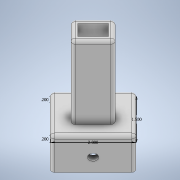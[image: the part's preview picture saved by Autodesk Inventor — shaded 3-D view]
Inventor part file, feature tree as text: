
AUTODESK INVENTOR PART (.ipt)
format: ipt  version: 2020 (Build 240168000, 168)  size: 212,480 bytes
history: native  units: in
note: dims shown in document units (in); Inventor stores cm internally (conversion verified against a paired STEP export)
features: sketch x4, extrude x4, hole x1, fillet x1
ambient origin geometry x8: Origin, YZ Plane, XZ Plane, XY Plane, X Axis, Y Axis, Z Axis, Center Point
bodies: Solid1 (feature_tree)
feature tree (10):
  sketch  "Sketch1"  dims[d0=1.5in d1=2.0in]
  extrude  "Extrusion1"  Depth=2.0in
  extrude  "Extrusion2"  Depth=0.2in
  hole  "Hole1"  [1 undecoded]
  extrude  "Extrusion3"  Depth=1.0in
  extrude  "Extrusion4"  Depth=0.7441in
  fillet  "Fillet1"  Radius=1.0276in
  sketch  "Sketch2"  dims[d2=0.2in d3=0.2in]
  sketch  "Sketch3"  dims[d4=1.0in d5=0.0in d6=0.2in d7=0.0in]
  sketch  "Sketch4"  dims[d8=0.5in d9=0.266in d10=0.75in d11=0.438in d12=0.25in d13=0.5635in d14=1.0in d15=0.8108in d16=1.0in d17=0.7441in d18=1.0276in d19=0.4291in d20=0.7126in d21=2.75in d22=0.0in d23=0.372in d24=1.0in d25=0.25in d26=3.0in d27=0.0in d28=0.1in]
note: 1 required parameter value undecoded (feature->parameter linkage not recoverable at this tier; creation-order binding heuristic only, values carry confidence <= 0.55)
